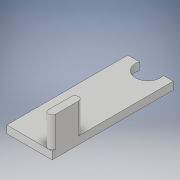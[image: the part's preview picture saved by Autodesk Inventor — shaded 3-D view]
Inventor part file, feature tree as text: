
AUTODESK INVENTOR PART (.ipt)
format: ipt  version: 2018 (Build 220112000, 112)  size: 119,296 bytes
history: native  units: in
note: dims shown in document units (in); Inventor stores cm internally (conversion verified against a paired STEP export)
features: extrude x2, sketch x2, hole x1
ambient origin geometry x8: Origin, YZ Plane, XZ Plane, XY Plane, X Axis, Y Axis, Z Axis, Center Point
bodies: Solid1 (feature_tree)
feature tree (5):
  extrude  "Extrusion1"  Depth=2.0in
  extrude  "Extrusion2"  Depth=0.5in TaperAngle=0.0deg
  hole  "Hole1"  [1 undecoded]
  sketch  "Sketch1"  dims[d1=0.75in d4=2.0in]
  sketch  "Sketch2"  dims[d5=0.125in d6=0.0in d7=0.5in d8=0.0in d11=0.5in d12=0.125in d13=0.375in d23=0.0625in d24=0.0625in d25=0.375in d26=0.0in d27=1.0in d28=1.0in d29=0.4118in d30=0.75in d31=0.375in d32=0.25in d33=0.5635in d34=1.0in d35=0.8108in]
note: 1 required parameter value undecoded (feature->parameter linkage not recoverable at this tier; creation-order binding heuristic only, values carry confidence <= 0.55)
